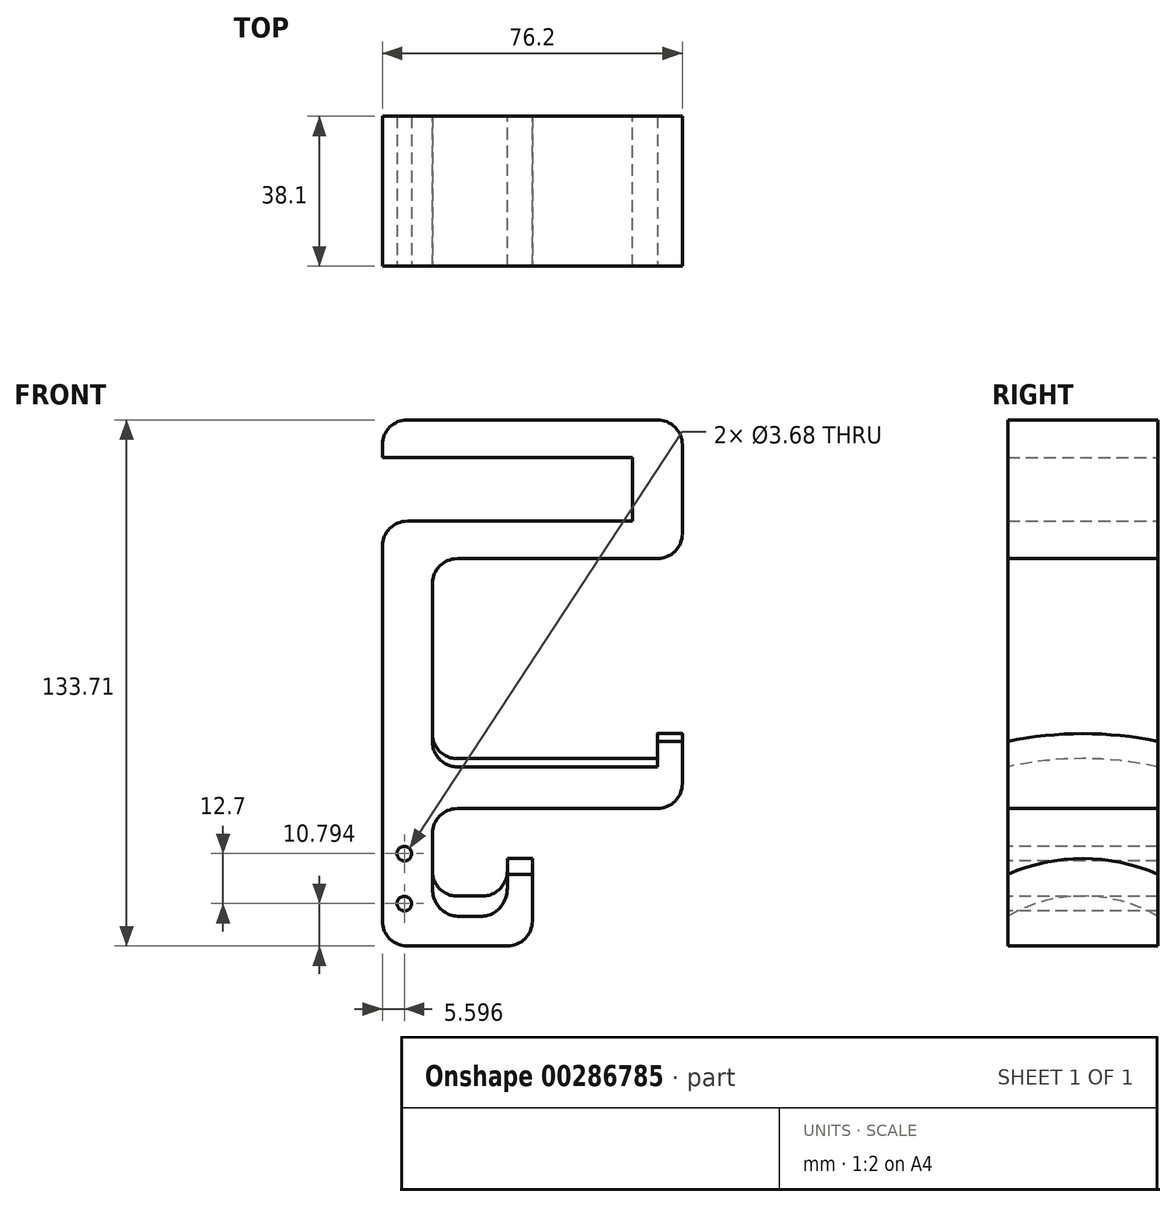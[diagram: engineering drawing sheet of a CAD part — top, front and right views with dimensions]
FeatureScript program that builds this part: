
annotation { "Feature Type Name" : "Feature", "Feature Type Description" : "" }
export const myFeature = defineFeature(function(context is Context, id is Id, definition is map)
    precondition{}
    {
        {
            var Q0;
            Q0=qCreatedBy(makeId("Front.planeOp"),FACE);
            var sketch = newSketch(context, id + "F0", { "sketchPlane" : qUnion([Q0])});
            skLineSegment(sketch, "E0", {"start": v(0, 0) * mm, "end": v(-63.5, 0) * mm});
            skLineSegment(sketch, "E1", {"start": v(-63.5, 0) * mm, "end": v(-63.5, 9.52) * mm});
            skLineSegment(sketch, "E2", {"start": v(-63.5, 9.53) * mm, "end": v(12.7, 9.53) * mm});
            skLineSegment(sketch, "E3", {"start": v(12.7, 9.53) * mm, "end": v(12.7, -25.76) * mm});
            skLineSegment(sketch, "E4", {"start": v(12.7, -25.76) * mm, "end": v(-50.8, -25.76) * mm});
            skLineSegment(sketch, "E5", {"start": v(-50.8, -25.76) * mm, "end": v(-50.8, -76.56) * mm});
            skLineSegment(sketch, "E6", {"start": v(-50.8, -76.56) * mm, "end": v(6.35, -76.56) * mm});
            skLineSegment(sketch, "E7", {"start": v(6.35, -76.56) * mm, "end": v(6.35, -70.2) * mm});
            skLineSegment(sketch, "E8", {"start": v(6.35, -70.2) * mm, "end": v(12.7, -70.2) * mm});
            skLineSegment(sketch, "E9", {"start": v(12.7, -70.2) * mm, "end": v(12.7, -89.26) * mm});
            skLineSegment(sketch, "E10", {"start": v(12.7, -89.26) * mm, "end": v(-50.8, -89.26) * mm});
            skLineSegment(sketch, "E11", {"start": v(-50.8, -89.26) * mm, "end": v(-50.8, -111.48) * mm});
            skLineSegment(sketch, "E12", {"start": v(-50.8, -111.48) * mm, "end": v(-31.75, -111.48) * mm});
            skLineSegment(sketch, "E13", {"start": v(-31.75, -111.48) * mm, "end": v(-31.75, -101.96) * mm});
            skLineSegment(sketch, "E14", {"start": v(-31.75, -101.96) * mm, "end": v(-25.4, -101.96) * mm});
            skLineSegment(sketch, "E15", {"start": v(-25.4, -101.96) * mm, "end": v(-25.4, -124.18) * mm});
            skLineSegment(sketch, "E16", {"start": v(-25.4, -124.18) * mm, "end": v(-63.5, -124.18) * mm});
            skLineSegment(sketch, "E17", {"start": v(-63.5, -124.18) * mm, "end": v(-63.5, -16.23) * mm});
            skLineSegment(sketch, "E18", {"start": v(-63.5, -16.23) * mm, "end": v(0, -16.23) * mm});
            skLineSegment(sketch, "E19", {"start": v(0, -16.23) * mm, "end": v(0, 0) * mm});
            skSolve(sketch);
        }
        {
            var Q0;
            Q0 = qSketchRegion(id + "F0", true);
            extrude(context, id + "F1", {"entities" : qUnion([Q0]), "endBound" : BoundingType.SYMMETRIC, "offsetDistance" : 25.4 * mm, "depth" : 38.1 * mm});
        }
        {
            var Q0;
            Q0=qCreatedBy(makeId("Front.planeOp"),FACE);
            var sketch = newSketch(context, id + "F2", { "sketchPlane" : qUnion([Q0])});
            skLineSegment(sketch, "E20", {"start": v(-50.8, -76.56) * mm, "end": v(6.35, -76.56) * mm});
            skLineSegment(sketch, "E21", {"start": v(6.35, -76.56) * mm, "end": v(6.35, -70.2) * mm});
            skLineSegment(sketch, "E22", {"start": v(12.7, -57.5) * mm, "end": v(-50.8, -57.5) * mm});
            skLineSegment(sketch, "E23", {"start": v(-50.8, -57.5) * mm, "end": v(-50.8, -76.56) * mm});
            skLineSegment(sketch, "E24", {"start": v(-74.62, -165.46) * mm, "end": v(33.74, -165.46) * mm, "construction": true});
            skLineSegment(sketch, "E25", {"start": v(6.35, -70.2) * mm, "end": v(12.7, -70.2) * mm});
            skLineSegment(sketch, "E26", {"start": v(12.7, -70.2) * mm, "end": v(12.7, -57.5) * mm});
            skSolve(sketch);
        }
        {
            var Q0;
            Q0 = qSketchRegion(id + "F2", true);
            var Q1;
            Q1=sQuery(id+"F2.wireOp",EDGE,"E24");
            revolve(context, id + "F3", {"operationType" : NewBodyOperationType.REMOVE, "entities" : qUnion([Q0]), "axis" : qUnion([Q1]), "revolveType" : RevolveType.FULL, "oppositeDirection" : true});
        }
        {
            var Q0;
            Q0=qCreatedBy(makeId("Front.planeOp"),FACE);
            var sketch = newSketch(context, id + "F4", { "sketchPlane" : qUnion([Q0])});
            skLineSegment(sketch, "E27.0", {"start": v(-50.8, -111.48) * mm, "end": v(-31.75, -111.48) * mm});
            skLineSegment(sketch, "E28", {"start": v(-31.75, -111.48) * mm, "end": v(-31.75, -101.96) * mm});
            skLineSegment(sketch, "E29", {"start": v(-50.8, -89.26) * mm, "end": v(-50.8, -111.48) * mm});
            skLineSegment(sketch, "E30", {"start": v(-50.8, -149.58) * mm, "end": v(-31.75, -149.58) * mm, "construction": true});
            skLineSegment(sketch, "E31", {"start": v(-50.8, -89.26) * mm, "end": v(-25.4, -89.26) * mm});
            skLineSegment(sketch, "E32", {"start": v(-25.4, -89.26) * mm, "end": v(-25.4, -101.96) * mm});
            skLineSegment(sketch, "E33.0", {"start": v(-31.75, -101.96) * mm, "end": v(-25.4, -101.96) * mm});
            skSolve(sketch);
        }
        {
            var Q0;
            Q0=makeQuery(id+"F4.imprint","IMPRINT",FACE,{"disambiguationData":[TD([[makeQuery(id+"F4.imprint","IMPRINT",EDGE,{"derivedFrom":sQuery(id+"F4.wireOp",EDGE,"E27.0")}),1.0]])]});
            var Q1;
            Q1=sQuery(id+"F4.wireOp",EDGE,"E30");
            revolve(context, id + "F5", {"operationType" : NewBodyOperationType.REMOVE, "entities" : qUnion([Q0]), "axis" : qUnion([Q1]), "revolveType" : RevolveType.FULL, "oppositeDirection" : true});
        }
        {
            var Q0;
            Q0=makeQuery(id+"F1.opExtrude","SWEPT_EDGE",EDGE,{"disambiguationData":[OSD([sQuery(id+"F0.wireOp",EDGE,"E2"),sQuery(id+"F0.wireOp",EDGE,"E3")])]});
            var Q1;
            Q1=makeQuery(id+"F1.opExtrude","SWEPT_EDGE",EDGE,{"disambiguationData":[OSD([sQuery(id+"F0.wireOp",EDGE,"E1"),sQuery(id+"F0.wireOp",EDGE,"E2")])]});
            var Q2;
            Q2=makeQuery(id+"F1.opExtrude","SWEPT_EDGE",EDGE,{"disambiguationData":[OSD([sQuery(id+"F0.wireOp",EDGE,"E17"),sQuery(id+"F0.wireOp",EDGE,"E18")])]});
            var Q3;
            Q3=makeQuery(id+"F1.opExtrude","SWEPT_EDGE",EDGE,{"disambiguationData":[OSD([sQuery(id+"F0.wireOp",EDGE,"E3"),sQuery(id+"F0.wireOp",EDGE,"E4")])]});
            var Q4;
            Q4=makeQuery(id+"F1.opExtrude","SWEPT_EDGE",EDGE,{"disambiguationData":[OSD([sQuery(id+"F0.wireOp",EDGE,"E4"),sQuery(id+"F0.wireOp",EDGE,"E5")])]});
            var Q5;
            Q5=makeQuery(id+"F3.boolean.opBoolean","COPY",EDGE,{"derivedFrom":makeQuery(id+"F3.opRevolve","SWEPT_EDGE",EDGE,{"disambiguationData":[OSD([sQuery(id+"F2.wireOp",EDGE,"E20"),sQuery(id+"F2.wireOp",EDGE,"E23")])]})});
            var Q6;
            Q6=makeQuery(id+"F1.opExtrude","SWEPT_EDGE",EDGE,{"disambiguationData":[OSD([sQuery(id+"F0.wireOp",EDGE,"E11"),sQuery(id+"F0.wireOp",EDGE,"E12")])]});
            var Q7;
            Q7=makeQuery(id+"F1.opExtrude","SWEPT_EDGE",EDGE,{"disambiguationData":[OSD([sQuery(id+"F0.wireOp",EDGE,"E12"),sQuery(id+"F0.wireOp",EDGE,"E13")])]});
            var Q8;
            Q8=makeQuery(id+"F1.opExtrude","SWEPT_EDGE",EDGE,{"disambiguationData":[OSD([sQuery(id+"F0.wireOp",EDGE,"E16"),sQuery(id+"F0.wireOp",EDGE,"E17")])]});
            var Q9;
            Q9=makeQuery(id+"F1.opExtrude","SWEPT_EDGE",EDGE,{"disambiguationData":[OSD([sQuery(id+"F0.wireOp",EDGE,"E15"),sQuery(id+"F0.wireOp",EDGE,"E16")])]});
            var Q10;
            Q10=makeQuery(id+"F1.opExtrude","SWEPT_EDGE",EDGE,{"disambiguationData":[OSD([sQuery(id+"F0.wireOp",EDGE,"E9"),sQuery(id+"F0.wireOp",EDGE,"E10")])]});
            var Q11;
            Q11=makeQuery(id+"F1.opExtrude","SWEPT_EDGE",EDGE,{"disambiguationData":[OSD([sQuery(id+"F0.wireOp",EDGE,"E10"),sQuery(id+"F0.wireOp",EDGE,"E11")])]});
            var Q12;
            Q12=makeQuery(id+"F5.boolean.opBoolean","COPY",EDGE,{"derivedFrom":makeQuery(id+"F5.opRevolve","SWEPT_EDGE",EDGE,{"disambiguationData":[OSD([sQuery(id+"F4.wireOp",EDGE,"E27.0"),sQuery(id+"F4.wireOp",EDGE,"E29")])]})});
            var Q13;
            Q13=makeQuery(id+"F5.boolean.opBoolean","COPY",EDGE,{"derivedFrom":makeQuery(id+"F5.opRevolve","SWEPT_EDGE",EDGE,{"disambiguationData":[OSD([sQuery(id+"F4.wireOp",EDGE,"E27.0"),sQuery(id+"F4.wireOp",EDGE,"E28")])]})});
            fillet(context, id + "F6", {"entities" : qUnion([Q0, Q1, Q2, Q3, Q4, Q5, Q6, Q7, Q8, Q9, Q10, Q11, Q12, Q13]), "radius" : 6.35 * mm, "tangentPropagation" : true, "allowEdgeOverflow" : false});
        }
        {
            var Q0;
            Q0=makeQuery(id+"F1.opExtrude","CAP_FACE",FACE,{"disambiguationData":[OSD([sQuery(id+"F0.wireOp",EDGE,"E0"),sQuery(id+"F0.wireOp",EDGE,"E1"),sQuery(id+"F0.wireOp",EDGE,"E2"),sQuery(id+"F0.wireOp",EDGE,"E3"),sQuery(id+"F0.wireOp",EDGE,"E4"),sQuery(id+"F0.wireOp",EDGE,"E5"),sQuery(id+"F0.wireOp",EDGE,"E6"),sQuery(id+"F0.wireOp",EDGE,"E7"),sQuery(id+"F0.wireOp",EDGE,"E8"),sQuery(id+"F0.wireOp",EDGE,"E9"),sQuery(id+"F0.wireOp",EDGE,"E10"),sQuery(id+"F0.wireOp",EDGE,"E11"),sQuery(id+"F0.wireOp",EDGE,"E12"),sQuery(id+"F0.wireOp",EDGE,"E13"),sQuery(id+"F0.wireOp",EDGE,"E14"),sQuery(id+"F0.wireOp",EDGE,"E15"),sQuery(id+"F0.wireOp",EDGE,"E16"),sQuery(id+"F0.wireOp",EDGE,"E17"),sQuery(id+"F0.wireOp",EDGE,"E18"),sQuery(id+"F0.wireOp",EDGE,"E19")])],"isStart":false});
            var sketch = newSketch(context, id + "F7", { "sketchPlane" : qUnion([Q0])});
            skCircle(sketch, "E34", {"center": v(-57.9, -100.69) * mm, "radius": 1.84 * mm});
            skCircle(sketch, "E35", {"center": v(-57.9, -113.39) * mm, "radius": 1.84 * mm});
            skLineSegment(sketch, "E36", {"start": v(-57.9, -113.39) * mm, "end": v(-57.9, -100.69) * mm, "construction": true});
            skPoint(sketch, "E37", {"position": v(-57.9, -107.04) * mm});
            skLineSegment(sketch, "E38", {"start": v(-63.5, -107.04) * mm, "end": v(-52.3, -107.04) * mm, "construction": true});
            skSolve(sketch);
        }
        {
            var Q0;
            Q0 = qSketchRegion(id + "F7", true);
            extrude(context, id + "F8", {"entities" : qUnion([Q0]), "operationType" : NewBodyOperationType.REMOVE, "endBound" : BoundingType.THROUGH_ALL, "oppositeDirection" : true, "depth" : 25.4 * mm});
        }
    });
